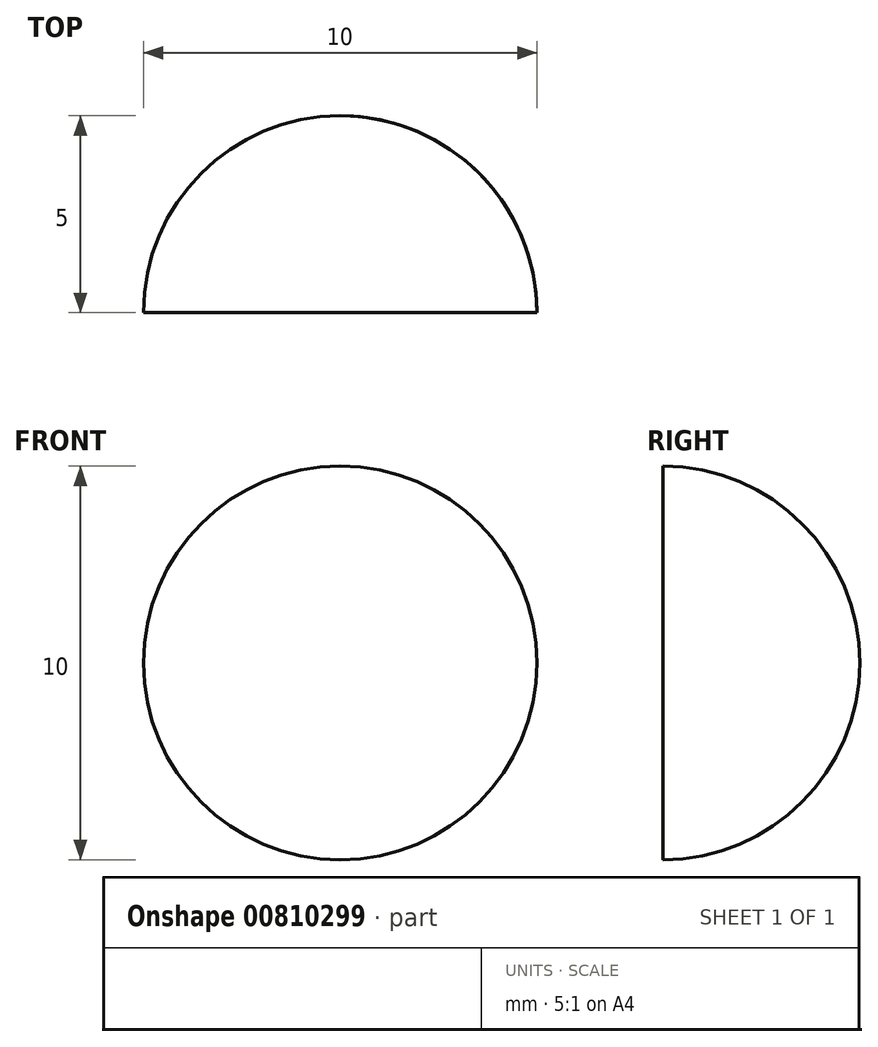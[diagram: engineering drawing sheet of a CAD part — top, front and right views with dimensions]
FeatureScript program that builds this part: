
annotation { "Feature Type Name" : "Feature", "Feature Type Description" : "" }
export const myFeature = defineFeature(function(context is Context, id is Id, definition is map)
    precondition{}
    {
        {
            var Q0;
            Q0=qCreatedBy(makeId("Top.planeOp"),FACE);
            var sketch = newSketch(context, id + "F0", { "sketchPlane" : qUnion([Q0])});
            skLineSegment(sketch, "E0", {"start": v(0, 0) * mm, "end": v(5, 0) * mm});
            skLineSegment(sketch, "E1", {"start": v(5, 0) * mm, "end": v(5, 5) * mm});
            skArc(sketch, "E2", {"start": v(5, 5) * mm, "mid": v(1.46, 3.54) * mm, "end": v(0, 0) * mm});
            skSolve(sketch);
        }
        {
            var Q0;
            Q0=makeQuery(id+"F0.imprint","IMPRINT",FACE,{"disambiguationData":[TD([[makeQuery(id+"F0.imprint","IMPRINT",EDGE,{"derivedFrom":sQuery(id+"F0.wireOp",EDGE,"E0")}),1.0]])]});
            var Q1;
            Q1=sQuery(id+"F0.wireOp",EDGE,"E1");
            revolve(context, id + "F1", {"surfaceOperationType" : NewSurfaceOperationType.NEW, "entities" : qUnion([Q0]), "axis" : qUnion([Q1]), "revolveType" : RevolveType.FULL});
        }
    });
